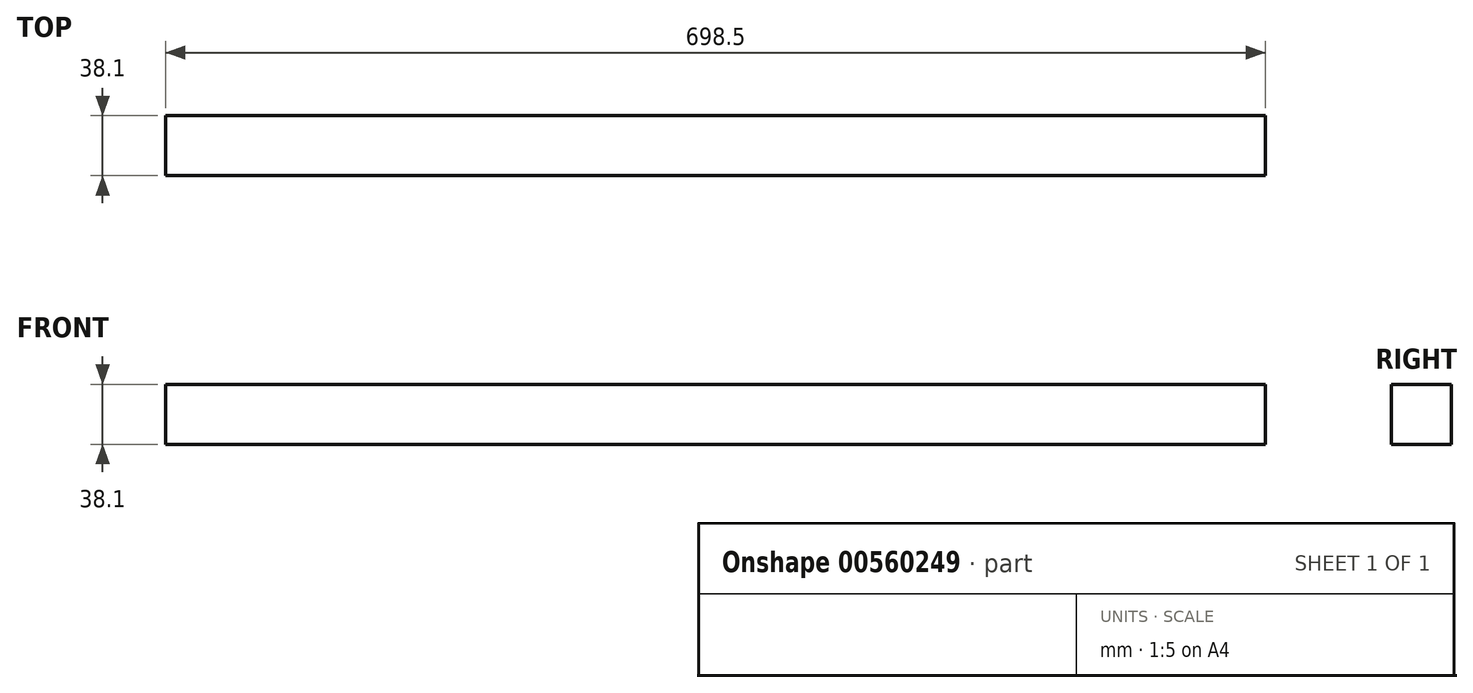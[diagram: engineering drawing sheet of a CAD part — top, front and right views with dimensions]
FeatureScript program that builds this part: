
annotation { "Feature Type Name" : "Feature", "Feature Type Description" : "" }
export const myFeature = defineFeature(function(context is Context, id is Id, definition is map)
    precondition{}
    {
        {
            var Q0;
            Q0=qCreatedBy(makeId("Front.planeOp"),FACE);
            var sketch = newSketch(context, id + "F0", { "sketchPlane" : qUnion([Q0])});
            skLineSegment(sketch, "E0.bottom", {"start": v(-349.25, 19.05) * mm, "end": v(349.25, 19.05) * mm});
            skLineSegment(sketch, "E0.top", {"start": v(-349.25, -19.05) * mm, "end": v(349.25, -19.05) * mm});
            skLineSegment(sketch, "E0.left", {"start": v(-349.25, 19.05) * mm, "end": v(-349.25, -19.05) * mm});
            skLineSegment(sketch, "E0.right", {"start": v(349.25, 19.05) * mm, "end": v(349.25, -19.05) * mm});
            skSolve(sketch);
        }
        {
            var Q0;
            Q0=makeQuery(id+"F0.imprint","IMPRINT",FACE,{"disambiguationData":[TD([[makeQuery(id+"F0.imprint","IMPRINT",EDGE,{"derivedFrom":sQuery(id+"F0.wireOp",EDGE,"E0.bottom")}),-1.0]])]});
            extrude(context, id + "F1", {"entities" : qUnion([Q0]), "depth" : 38.1 * mm, "offsetDistance" : 25.4 * mm});
        }
    });
